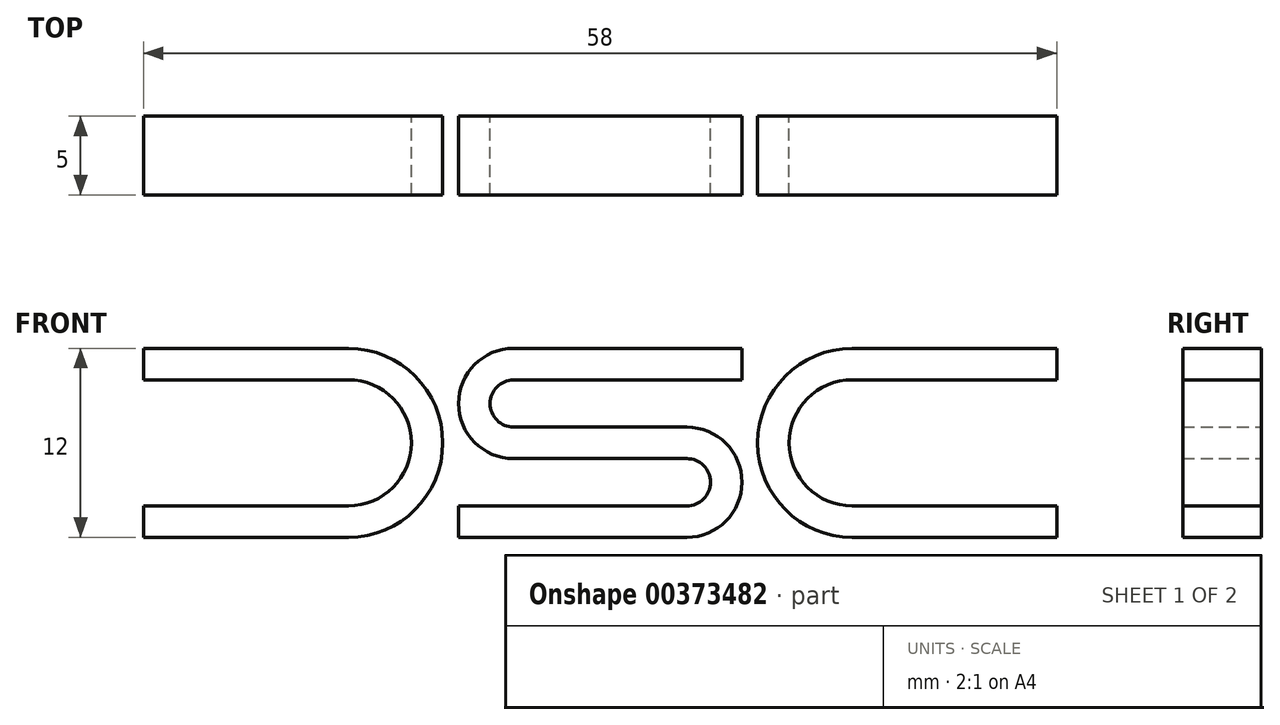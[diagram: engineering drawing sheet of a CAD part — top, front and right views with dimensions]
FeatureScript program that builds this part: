
annotation { "Feature Type Name" : "Feature", "Feature Type Description" : "" }
export const myFeature = defineFeature(function(context is Context, id is Id, definition is map)
    precondition{}
    {
        {
            var Q0;
            Q0=qCreatedBy(makeId("Front.planeOp"),FACE);
            var sketch = newSketch(context, id + "F0", { "sketchPlane" : qUnion([Q0])});
            skLineSegment(sketch, "E0.bottom", {"start": v(24, 6) * mm, "end": v(11, 6) * mm});
            skLineSegment(sketch, "E0.top", {"start": v(24, -6) * mm, "end": v(11, -6) * mm});
            skLineSegment(sketch, "E0.left", {"start": v(30, 0) * mm, "end": v(30, 0) * mm});
            skLineSegment(sketch, "E0.right", {"start": v(-30, 0) * mm, "end": v(-30, 0) * mm});
            skPoint(sketch, "E0.middle", {"position": v(0, 0) * mm});
            skPoint(sketch, "E1.visualSharp", {"position": v(-30, 6) * mm});
            skArc(sketch, "E1.filletArc", {"start": v(-24, 6) * mm, "mid": v(-28.24, 4.24) * mm, "end": v(-30, 0) * mm});
            skPoint(sketch, "E2.visualSharp", {"position": v(-30, -6) * mm});
            skArc(sketch, "E2.filletArc", {"start": v(-30, 0) * mm, "mid": v(-28.24, -4.24) * mm, "end": v(-24, -6) * mm});
            skPoint(sketch, "E3.visualSharp", {"position": v(30, 6) * mm});
            skArc(sketch, "E3.filletArc", {"start": v(30, 0) * mm, "mid": v(28.24, 4.24) * mm, "end": v(24, 6) * mm});
            skPoint(sketch, "E4.visualSharp", {"position": v(30, -6) * mm});
            skArc(sketch, "E4.filletArc", {"start": v(24, -6) * mm, "mid": v(28.24, -4.24) * mm, "end": v(30, 0) * mm});
            skArc(sketch, "E5.0", {"start": v(-24, 4) * mm, "mid": v(-26.83, 2.83) * mm, "end": v(-28, 0) * mm});
            skArc(sketch, "E6.MirrorCS", {"start": v(-24, -4) * mm, "mid": v(-26.83, -2.83) * mm, "end": v(-28, 0) * mm});
            skArc(sketch, "E7.MirrorCS", {"start": v(24, 4) * mm, "mid": v(26.83, 2.83) * mm, "end": v(28, 0) * mm});
            skArc(sketch, "E8.MirrorCS", {"start": v(24, -4) * mm, "mid": v(26.83, -2.83) * mm, "end": v(28, 0) * mm});
            skLineSegment(sketch, "E9", {"start": v(-24, 4) * mm, "end": v(-11, 4) * mm});
            skLineSegment(sketch, "E10", {"start": v(-24, -4) * mm, "end": v(-11, -4) * mm});
            skLineSegment(sketch, "E11", {"start": v(-11, 6) * mm, "end": v(-11, 4) * mm});
            skLineSegment(sketch, "E12.MirrorCS", {"start": v(11, 6) * mm, "end": v(11, 4) * mm});
            skLineSegment(sketch, "E13.trimOffspring", {"start": v(-11, 6) * mm, "end": v(-24, 6) * mm});
            skLineSegment(sketch, "E14.trimOffspring", {"start": v(-5.5, 4) * mm, "end": v(9, 4) * mm});
            skLineSegment(sketch, "E15.trimOffspring", {"start": v(-11, -4) * mm, "end": v(-11, -6) * mm});
            skLineSegment(sketch, "E16.trimOffspring", {"start": v(-9, -4) * mm, "end": v(5.5, -4) * mm});
            skLineSegment(sketch, "E17.trimOffspring", {"start": v(-11, -6) * mm, "end": v(-24, -6) * mm});
            skLineSegment(sketch, "E18.trimOffspring", {"start": v(9, 6) * mm, "end": v(-5.5, 6) * mm});
            skLineSegment(sketch, "E19.trimOffspring", {"start": v(11, 4) * mm, "end": v(24, 4) * mm});
            skLineSegment(sketch, "E20.trimOffspring", {"start": v(11, -4) * mm, "end": v(24, -4) * mm});
            skLineSegment(sketch, "E21.trimOffspring", {"start": v(5.5, -6) * mm, "end": v(-9, -6) * mm});
            skLineSegment(sketch, "E22.trimOffspring", {"start": v(11, -4) * mm, "end": v(11, -6) * mm});
            skLineSegment(sketch, "E23.MirrorCS", {"start": v(-5.5, -1) * mm, "end": v(5.5, -1) * mm});
            skLineSegment(sketch, "E24", {"start": v(-9, 2.5) * mm, "end": v(9, 2.5) * mm, "construction": true});
            skLineSegment(sketch, "E25", {"start": v(-9, -2.5) * mm, "end": v(9, -2.5) * mm, "construction": true});
            skArc(sketch, "E26", {"start": v(-5.5, 6) * mm, "mid": v(-9, 2.5) * mm, "end": v(-5.5, -1) * mm});
            skArc(sketch, "E27", {"start": v(-5.5, 4) * mm, "mid": v(-7, 2.5) * mm, "end": v(-5.5, 1) * mm});
            skArc(sketch, "E28", {"start": v(5.5, -6) * mm, "mid": v(9, -2.5) * mm, "end": v(5.5, 1) * mm});
            skArc(sketch, "E29", {"start": v(5.5, -4) * mm, "mid": v(7, -2.5) * mm, "end": v(5.5, -1) * mm});
            skPoint(sketch, "E30.orphan", {"position": v(-9, 6) * mm});
            skPoint(sketch, "E31.orphan", {"position": v(-9, 4) * mm});
            skLineSegment(sketch, "E32.trimOffspring", {"start": v(-5.5, 1) * mm, "end": v(5.5, 1) * mm});
            skPoint(sketch, "E33.start.orphan", {"position": v(-9, 1) * mm});
            skLineSegment(sketch, "E34", {"start": v(9, 6) * mm, "end": v(9, 4) * mm});
            skLineSegment(sketch, "E35", {"start": v(-9, -4) * mm, "end": v(-9, -6) * mm});
            skPoint(sketch, "E36.orphan", {"position": v(-9, -1) * mm});
            skPoint(sketch, "E37.start.orphan", {"position": v(9, 1) * mm});
            skPoint(sketch, "E38.orphan", {"position": v(9, -6) * mm});
            skPoint(sketch, "E39.orphan", {"position": v(9, -1) * mm});
            skPoint(sketch, "E40.orphan", {"position": v(9, -4) * mm});
            skSolve(sketch);
        }
        {
            var Q0;
            Q0=makeQuery(id+"F0.imprint","IMPRINT",FACE,{"disambiguationData":[TD([[makeQuery(id+"F0.imprint","IMPRINT",EDGE,{"derivedFrom":sQuery(id+"F0.wireOp",EDGE,"E1.filletArc")}),1.0]])]});
            var Q1;
            Q1=makeQuery(id+"F0.imprint","IMPRINT",FACE,{"disambiguationData":[TD([[makeQuery(id+"F0.imprint","IMPRINT",EDGE,{"derivedFrom":sQuery(id+"F0.wireOp",EDGE,"E14.trimOffspring")}),1.0]])]});
            var Q2;
            Q2=makeQuery(id+"F0.imprint","IMPRINT",FACE,{"disambiguationData":[TD([[makeQuery(id+"F0.imprint","IMPRINT",EDGE,{"derivedFrom":sQuery(id+"F0.wireOp",EDGE,"E0.bottom")}),1.0]])]});
            extrude(context, id + "F1", {"entities" : qUnion([Q0, Q1, Q2]), "depth" : 5 * mm});
        }
        {
            var Q0;
            Q0=makeQuery(id+"F1.opExtrude","SWEPT_BODY",BODY,{"disambiguationData":[OSD([sQuery(id+"F0.wireOp",EDGE,"E1.filletArc"),sQuery(id+"F0.wireOp",EDGE,"E2.filletArc"),sQuery(id+"F0.wireOp",EDGE,"E6.MirrorCS"),sQuery(id+"F0.wireOp",EDGE,"E5.0"),sQuery(id+"F0.wireOp",EDGE,"E9"),sQuery(id+"F0.wireOp",EDGE,"E10"),sQuery(id+"F0.wireOp",EDGE,"E11"),sQuery(id+"F0.wireOp",EDGE,"E13.trimOffspring"),sQuery(id+"F0.wireOp",EDGE,"E15.trimOffspring"),sQuery(id+"F0.wireOp",EDGE,"E17.trimOffspring")])]});
            var Q1;
            Q1=makeQuery(id+"F1.opExtrude","CAP_EDGE",EDGE,{"disambiguationData":[OSD([sQuery(id+"F0.wireOp",EDGE,"E10")])],"isStart":false});
            transform(context, id + "F2", {"entities" : qUnion([Q0]), "transformType" : TransformType.TRANSLATION_DISTANCE, "transformDirection" : qUnion([Q1]), "distance" : 40 * mm, "makeCopy" : false});
        }
        {
            var Q0;
            Q0=makeQuery(id+"F1.opExtrude","SWEPT_BODY",BODY,{"disambiguationData":[OSD([sQuery(id+"F0.wireOp",EDGE,"E0.bottom"),sQuery(id+"F0.wireOp",EDGE,"E0.top"),sQuery(id+"F0.wireOp",EDGE,"E3.filletArc"),sQuery(id+"F0.wireOp",EDGE,"E4.filletArc"),sQuery(id+"F0.wireOp",EDGE,"E7.MirrorCS"),sQuery(id+"F0.wireOp",EDGE,"E8.MirrorCS"),sQuery(id+"F0.wireOp",EDGE,"E12.MirrorCS"),sQuery(id+"F0.wireOp",EDGE,"E19.trimOffspring"),sQuery(id+"F0.wireOp",EDGE,"E20.trimOffspring"),sQuery(id+"F0.wireOp",EDGE,"E22.trimOffspring")])]});
            var Q1;
            Q1=makeQuery(id+"F1.opExtrude","CAP_EDGE",EDGE,{"disambiguationData":[OSD([sQuery(id+"F0.wireOp",EDGE,"E16.trimOffspring")])],"isStart":false});
            transform(context, id + "F3", {"entities" : qUnion([Q0]), "transformType" : TransformType.TRANSLATION_DISTANCE, "transformDirection" : qUnion([Q1]), "distance" : 40 * mm, "oppositeDirection" : true, "makeCopy" : false});
        }
        {
            var Q0;
            Q0=makeQuery(id+"F1.opExtrude","SWEPT_BODY",BODY,{"disambiguationData":[OSD([sQuery(id+"F0.wireOp",EDGE,"E0.bottom"),sQuery(id+"F0.wireOp",EDGE,"E0.top"),sQuery(id+"F0.wireOp",EDGE,"E3.filletArc"),sQuery(id+"F0.wireOp",EDGE,"E4.filletArc"),sQuery(id+"F0.wireOp",EDGE,"E7.MirrorCS"),sQuery(id+"F0.wireOp",EDGE,"E8.MirrorCS"),sQuery(id+"F0.wireOp",EDGE,"E12.MirrorCS"),sQuery(id+"F0.wireOp",EDGE,"E19.trimOffspring"),sQuery(id+"F0.wireOp",EDGE,"E20.trimOffspring"),sQuery(id+"F0.wireOp",EDGE,"E22.trimOffspring")])]});
            var Q1;
            Q1=makeQuery(id+"F1.opExtrude","SWEPT_BODY",BODY,{"disambiguationData":[OSD([sQuery(id+"F0.wireOp",EDGE,"E1.filletArc"),sQuery(id+"F0.wireOp",EDGE,"E2.filletArc"),sQuery(id+"F0.wireOp",EDGE,"E6.MirrorCS"),sQuery(id+"F0.wireOp",EDGE,"E5.0"),sQuery(id+"F0.wireOp",EDGE,"E9"),sQuery(id+"F0.wireOp",EDGE,"E10"),sQuery(id+"F0.wireOp",EDGE,"E11"),sQuery(id+"F0.wireOp",EDGE,"E13.trimOffspring"),sQuery(id+"F0.wireOp",EDGE,"E15.trimOffspring"),sQuery(id+"F0.wireOp",EDGE,"E17.trimOffspring")])]});
            var Q2;
            Q2=makeQuery(id+"F1.opExtrude","SWEPT_BODY",BODY,{"disambiguationData":[OSD([sQuery(id+"F0.wireOp",EDGE,"E14.trimOffspring"),sQuery(id+"F0.wireOp",EDGE,"E16.trimOffspring"),sQuery(id+"F0.wireOp",EDGE,"E18.trimOffspring"),sQuery(id+"F0.wireOp",EDGE,"E21.trimOffspring"),sQuery(id+"F0.wireOp",EDGE,"E23.MirrorCS"),sQuery(id+"F0.wireOp",EDGE,"E26"),sQuery(id+"F0.wireOp",EDGE,"E27"),sQuery(id+"F0.wireOp",EDGE,"E28"),sQuery(id+"F0.wireOp",EDGE,"E29"),sQuery(id+"F0.wireOp",EDGE,"E32.trimOffspring"),sQuery(id+"F0.wireOp",EDGE,"E34"),sQuery(id+"F0.wireOp",EDGE,"E35")])]});
            transform(context, id + "F4", {"entities" : qUnion([Q0, Q1, Q2]), "transformType" : TransformType.TRANSLATION_3D, "dx" : 0 * mm, "dy" : 0 * mm, "dz" : 8 * mm, "makeCopy" : false});
        }
    });
